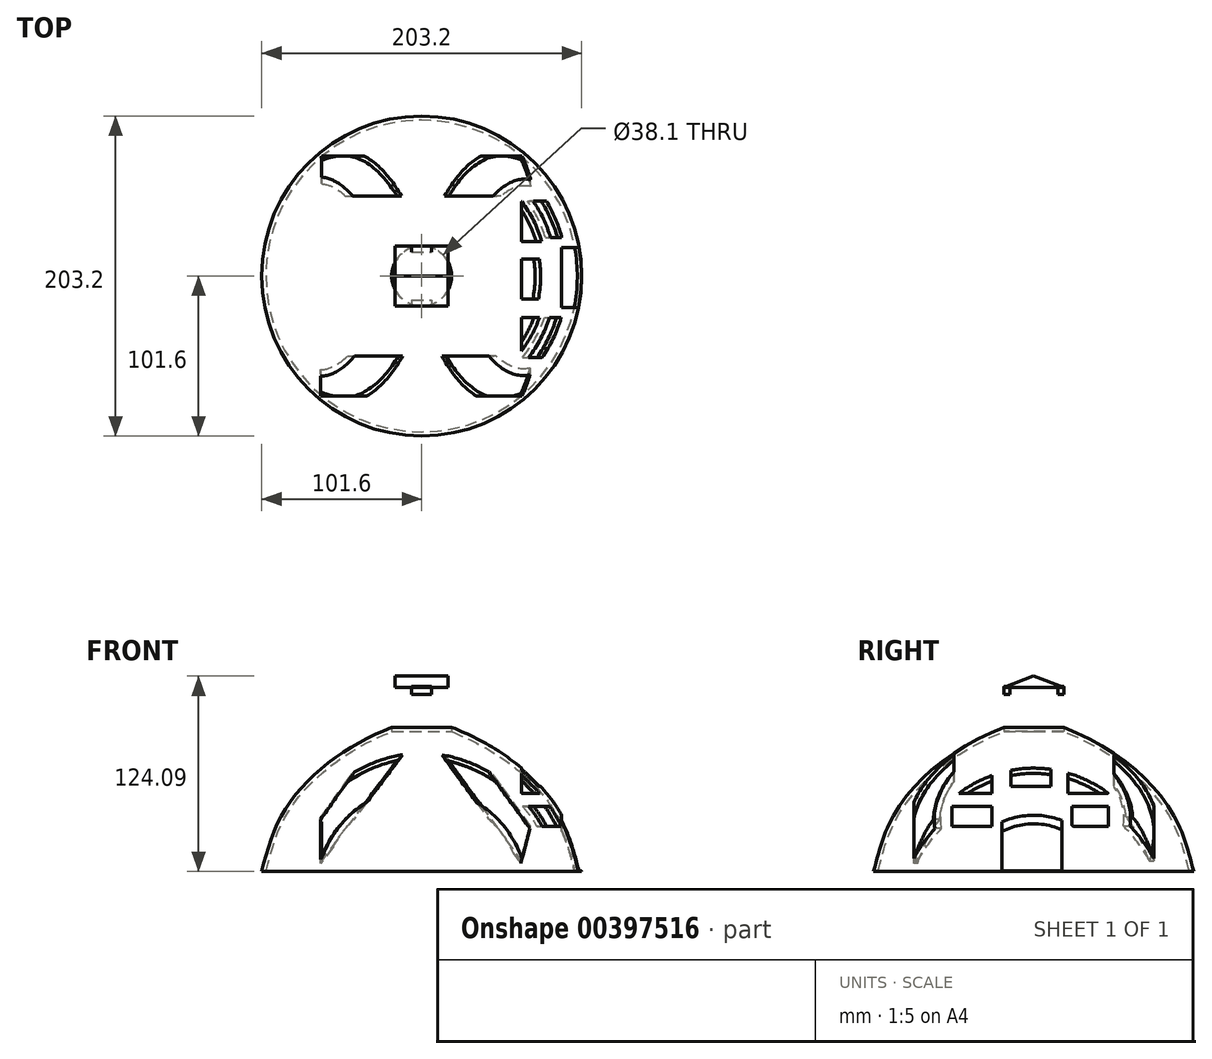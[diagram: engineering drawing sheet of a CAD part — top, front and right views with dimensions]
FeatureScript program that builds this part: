
annotation { "Feature Type Name" : "Feature", "Feature Type Description" : "" }
export const myFeature = defineFeature(function(context is Context, id is Id, definition is map)
    precondition{}
    {
        {
            var Q0;
            Q0=qCreatedBy(makeId("Top.planeOp"),FACE);
            var sketch = newSketch(context, id + "F0", { "sketchPlane" : qUnion([Q0])});
            skCircle(sketch, "E0", {"center": v(0, 0) * mm, "radius": 12.7 * mm});
            skSolve(sketch);
        }
        {
            var Q0;
            Q0=sQuery(id+"F0.wireOp",EDGE,"E0");
            extrude(context, id + "F1", {"bodyType" : ToolBodyType.SURFACE, "surfaceEntities" : qUnion([Q0]), "endBound" : BoundingType.SYMMETRIC, "oppositeDirection" : true, "depth" : 0.05 * mm});
        }
        {
            var Q0;
            Q0=qCreatedBy(makeId("Front.planeOp"),FACE);
            var sketch = newSketch(context, id + "F2", { "sketchPlane" : qUnion([Q0])});
            skLineSegment(sketch, "E1", {"start": v(0, -60.9) * mm, "end": v(101.6, -60.9) * mm});
            skLineSegment(sketch, "E2", {"start": v(0, -60.9) * mm, "end": v(0, -22.8) * mm});
            skFitSpline(sketch, "E3", {"points": [v(101.6, -60.9) * mm, v(91.03, -29.23) * mm, v(68.8, 0) * mm, v(35.83, 23) * mm, v(0, 37.82) * mm], "startDerivative": vector(-35.23, 136.52) * mm, "endDerivative": vector(-142.17, 51.79) * mm});
            skLineSegment(sketch, "E4", {"start": v(0, 37.82) * mm, "end": v(0, -22.8) * mm});
            skSolve(sketch);
        }
        {
            var Q0;
            Q0=makeQuery(id+"F2.imprint","IMPRINT",FACE,{"disambiguationData":[TD([[makeQuery(id+"F2.imprint","IMPRINT",EDGE,{"derivedFrom":sQuery(id+"F2.wireOp",EDGE,"E1")}),1.0]])]});
            var Q1;
            Q1=makeQuery(id+"F1.opExtrude","SWEPT_FACE",FACE,{"disambiguationData":[OSD([sQuery(id+"F0.wireOp",EDGE,"E0")])]});
            revolve(context, id + "F3", {"entities" : qUnion([Q0]), "axis" : qUnion([Q1]), "revolveType" : RevolveType.FULL});
        }
        {
            var Q0;
            Q0=makeQuery(id+"F3.opRevolve","SWEPT_FACE",FACE,{"disambiguationData":[OSD([sQuery(id+"F2.wireOp",EDGE,"E1")])]});
            shell(context, id + "F4", {"entities" : qUnion([Q0]), "thickness" : 2.54 * mm});
        }
        {
            var Q0;
            Q0=qCreatedBy(makeId("Right.planeOp"),FACE);
            cPlane(context, id + "F5", {"entities" : qUnion([Q0]), "cplaneType" : CPlaneType.OFFSET, "offset" : 88.9 * mm, "width" : 152.4 * mm, "height" : 152.4 * mm});
        }
        {
            var Q0;
            Q0=qCreatedBy(id+"F5.planeOp",FACE);
            var sketch = newSketch(context, id + "F6", { "sketchPlane" : qUnion([Q0])});
            skLineSegment(sketch, "E5", {"start": v(-20.07, -60.48) * mm, "end": v(18.03, -60.48) * mm});
            skLineSegment(sketch, "E6", {"start": v(-20.07, -60.48) * mm, "end": v(-20.07, -22.38) * mm});
            skLineSegment(sketch, "E7", {"start": v(18.03, -60.48) * mm, "end": v(18.03, -22.38) * mm});
            skArc(sketch, "E8", {"start": v(18.03, -22.38) * mm, "mid": v(-1.02, -11.63) * mm, "end": v(-20.07, -22.38) * mm});
            skSolve(sketch);
        }
        {
            var Q0;
            Q0 = qSketchRegion(id + "F6", true);
            extrude(context, id + "F7", {"entities" : qUnion([Q0]), "operationType" : NewBodyOperationType.REMOVE, "depth" : 25.4 * mm});
        }
        {
            var Q0;
            Q0=qCreatedBy(id+"F5.planeOp",FACE);
            var sketch = newSketch(context, id + "F8", { "sketchPlane" : qUnion([Q0])});
            skLineSegment(sketch, "E9", {"start": v(-26.48, -19.5) * mm, "end": v(-51.88, -19.5) * mm});
            skLineSegment(sketch, "E10", {"start": v(24.32, -19.5) * mm, "end": v(47.51, -19.5) * mm});
            skLineSegment(sketch, "E11", {"start": v(-51.88, -19.5) * mm, "end": v(-51.88, -32.2) * mm});
            skLineSegment(sketch, "E12", {"start": v(-26.48, -19.5) * mm, "end": v(-26.48, -32.2) * mm});
            skLineSegment(sketch, "E13", {"start": v(-51.88, -32.2) * mm, "end": v(-26.48, -32.2) * mm});
            skLineSegment(sketch, "E14", {"start": v(24.32, -19.5) * mm, "end": v(24.32, -32.2) * mm});
            skLineSegment(sketch, "E15", {"start": v(24.32, -32.2) * mm, "end": v(47.51, -32.2) * mm});
            skLineSegment(sketch, "E16", {"start": v(47.51, -32.2) * mm, "end": v(47.51, -19.5) * mm});
            skLineSegment(sketch, "E17.bottom", {"start": v(-51.88, 1.48) * mm, "end": v(-26.48, 1.48) * mm});
            skLineSegment(sketch, "E17.top", {"start": v(-51.88, -11.22) * mm, "end": v(-26.48, -11.22) * mm});
            skLineSegment(sketch, "E17.left", {"start": v(-51.88, 1.48) * mm, "end": v(-51.88, -11.22) * mm});
            skLineSegment(sketch, "E17.right", {"start": v(-26.48, 1.48) * mm, "end": v(-26.48, -11.22) * mm});
            skLineSegment(sketch, "E18.bottom", {"start": v(-14.57, 5.85) * mm, "end": v(10.83, 5.85) * mm});
            skLineSegment(sketch, "E18.top", {"start": v(-14.57, -6.85) * mm, "end": v(10.83, -6.85) * mm});
            skLineSegment(sketch, "E18.left", {"start": v(-14.57, 5.85) * mm, "end": v(-14.57, -6.85) * mm});
            skLineSegment(sketch, "E18.right", {"start": v(10.83, 5.85) * mm, "end": v(10.83, -6.85) * mm});
            skLineSegment(sketch, "E19.bottom", {"start": v(21.86, 1.48) * mm, "end": v(47.26, 1.48) * mm});
            skLineSegment(sketch, "E19.top", {"start": v(21.86, -11.22) * mm, "end": v(47.26, -11.22) * mm});
            skLineSegment(sketch, "E19.left", {"start": v(21.86, 1.48) * mm, "end": v(21.86, -11.22) * mm});
            skLineSegment(sketch, "E19.right", {"start": v(47.26, 1.48) * mm, "end": v(47.26, -11.22) * mm});
            skSolve(sketch);
        }
        {
            var Q0;
            Q0 = qSketchRegion(id + "F8", true);
            extrude(context, id + "F9", {"entities" : qUnion([Q0]), "operationType" : NewBodyOperationType.REMOVE, "oppositeDirection" : true, "depth" : 25.4 * mm});
        }
        {
            var Q0;
            Q0=qCreatedBy(makeId("Top.planeOp"),FACE);
            cPlane(context, id + "F10", {"entities" : qUnion([Q0]), "cplaneType" : CPlaneType.OFFSET, "offset" : 25.4 * mm, "width" : 152.4 * mm, "height" : 152.4 * mm});
        }
        {
            var Q0;
            Q0=qCreatedBy(id+"F10.planeOp",FACE);
            var sketch = newSketch(context, id + "F11", { "sketchPlane" : qUnion([Q0])});
            skCircle(sketch, "E20", {"center": v(0, 0) * mm, "radius": 19.05 * mm});
            skSolve(sketch);
        }
        {
            var Q0;
            Q0=sQuery(id+"F11.wireOp",EDGE,"E20");
            extrude(context, id + "F12", {"bodyType" : ToolBodyType.SURFACE, "surfaceEntities" : qUnion([Q0]), "depth" : 25.4 * mm});
        }
        {
            var Q0;
            Q0 = qSketchRegion(id + "F11", true);
            extrude(context, id + "F13", {"entities" : qUnion([Q0]), "operationType" : NewBodyOperationType.REMOVE, "depth" : 25.4 * mm});
        }
        {
            var Q0;
            Q0=qCreatedBy(makeId("Right.planeOp"),FACE);
            var sketch = newSketch(context, id + "F14", { "sketchPlane" : qUnion([Q0])});
            skLineSegment(sketch, "E21", {"start": v(19.11, 51.47) * mm, "end": v(19.11, 56.55) * mm});
            skLineSegment(sketch, "E22", {"start": v(-18.99, 51.47) * mm, "end": v(-18.99, 56.55) * mm});
            skLineSegment(sketch, "E23", {"start": v(19.11, 56.55) * mm, "end": v(15.3, 56.55) * mm});
            skLineSegment(sketch, "E24", {"start": v(15.3, 56.55) * mm, "end": v(15.3, 51.47) * mm});
            skLineSegment(sketch, "E25", {"start": v(-15.18, 56.55) * mm, "end": v(-15.18, 51.47) * mm});
            skLineSegment(sketch, "E26", {"start": v(15.3, 51.47) * mm, "end": v(19.11, 51.47) * mm});
            skLineSegment(sketch, "E27", {"start": v(-15.18, 51.47) * mm, "end": v(-18.99, 51.47) * mm});
            skLineSegment(sketch, "E28", {"start": v(-15.18, 56.55) * mm, "end": v(-18.99, 56.55) * mm});
            skSolve(sketch);
        }
        {
            var Q0;
            Q0 = qSketchRegion(id + "F14", true);
            extrude(context, id + "F15", {"entities" : qUnion([Q0]), "endBound" : BoundingType.SYMMETRIC, "oppositeDirection" : true, "depth" : 12.7 * mm});
        }
        {
            var Q0;
            Q0=qCreatedBy(makeId("Right.planeOp"),FACE);
            var sketch = newSketch(context, id + "F16", { "sketchPlane" : qUnion([Q0])});
            skLineSegment(sketch, "E29", {"start": v(-19.05, 56.1) * mm, "end": v(19.05, 56.1) * mm});
            skLineSegment(sketch, "E30", {"start": v(-19.05, 56.1) * mm, "end": v(0, 63.18) * mm});
            skLineSegment(sketch, "E31", {"start": v(0, 63.18) * mm, "end": v(19.05, 56.1) * mm});
            skSolve(sketch);
        }
        {
            var Q0;
            Q0 = qSketchRegion(id + "F16", true);
            extrude(context, id + "F17", {"entities" : qUnion([Q0]), "endBound" : BoundingType.SYMMETRIC, "depth" : 33.53 * mm});
        }
        {
            var Q0;
            Q0=qCreatedBy(makeId("Front.planeOp"),FACE);
            cPlane(context, id + "F18", {"entities" : qUnion([Q0]), "cplaneType" : CPlaneType.OFFSET, "offset" : 76.2 * mm, "width" : 152.4 * mm, "height" : 152.4 * mm});
        }
        {
            var Q0;
            Q0=qCreatedBy(id+"F18.planeOp",FACE);
            var sketch = newSketch(context, id + "F19", { "sketchPlane" : qUnion([Q0])});
            skLineSegment(sketch, "E32", {"start": v(-64.12, -55.82) * mm, "end": v(-64.12, -27.84) * mm});
            skLineSegment(sketch, "E33", {"start": v(-64.12, -27.84) * mm, "end": v(-30.03, 19.97) * mm});
            skLineSegment(sketch, "E34", {"start": v(-30.03, 19.97) * mm, "end": v(-6.97, 19.97) * mm});
            skLineSegment(sketch, "E35", {"start": v(-6.97, 19.97) * mm, "end": v(-64.12, -55.82) * mm});
            skLineSegment(sketch, "E36", {"start": v(7.87, 19.97) * mm, "end": v(62.96, -55.82) * mm});
            skLineSegment(sketch, "E37", {"start": v(62.96, -55.82) * mm, "end": v(68.79, -33.67) * mm});
            skLineSegment(sketch, "E38", {"start": v(68.79, -33.67) * mm, "end": v(29.8, 19.97) * mm});
            skLineSegment(sketch, "E39", {"start": v(29.8, 19.97) * mm, "end": v(7.87, 19.97) * mm});
            skSolve(sketch);
        }
        {
            var Q0;
            Q0 = qSketchRegion(id + "F19", true);
            extrude(context, id + "F20", {"entities" : qUnion([Q0]), "operationType" : NewBodyOperationType.REMOVE, "oppositeDirection" : true, "depth" : 25.4 * mm});
        }
        {
            var Q0;
            Q0=qCreatedBy(makeId("Front.planeOp"),FACE);
            cPlane(context, id + "F21", {"entities" : qUnion([Q0]), "cplaneType" : CPlaneType.OFFSET, "offset" : 76.2 * mm, "oppositeDirection" : true, "width" : 152.4 * mm, "height" : 152.4 * mm});
        }
        {
            var Q0;
            Q0=qCreatedBy(id+"F21.planeOp",FACE);
            var sketch = newSketch(context, id + "F22", { "sketchPlane" : qUnion([Q0])});
            skLineSegment(sketch, "E40", {"start": v(-63.73, -54.26) * mm, "end": v(-63.73, -26.27) * mm});
            skLineSegment(sketch, "E41", {"start": v(-63.73, -26.27) * mm, "end": v(-29.63, 21.53) * mm});
            skLineSegment(sketch, "E42", {"start": v(-29.63, 21.53) * mm, "end": v(-6.57, 21.53) * mm});
            skLineSegment(sketch, "E43", {"start": v(-6.57, 21.53) * mm, "end": v(-63.73, -54.26) * mm});
            skLineSegment(sketch, "E44", {"start": v(8.27, 21.53) * mm, "end": v(63.36, -54.26) * mm});
            skLineSegment(sketch, "E45", {"start": v(63.36, -54.26) * mm, "end": v(69.19, -32.1) * mm});
            skLineSegment(sketch, "E46", {"start": v(69.19, -32.1) * mm, "end": v(30.2, 21.53) * mm});
            skLineSegment(sketch, "E47", {"start": v(30.2, 21.53) * mm, "end": v(8.27, 21.53) * mm});
            skSolve(sketch);
        }
        {
            var Q0;
            Q0 = qSketchRegion(id + "F22", true);
            extrude(context, id + "F23", {"entities" : qUnion([Q0]), "operationType" : NewBodyOperationType.REMOVE, "depth" : 25.4 * mm});
        }
    });
